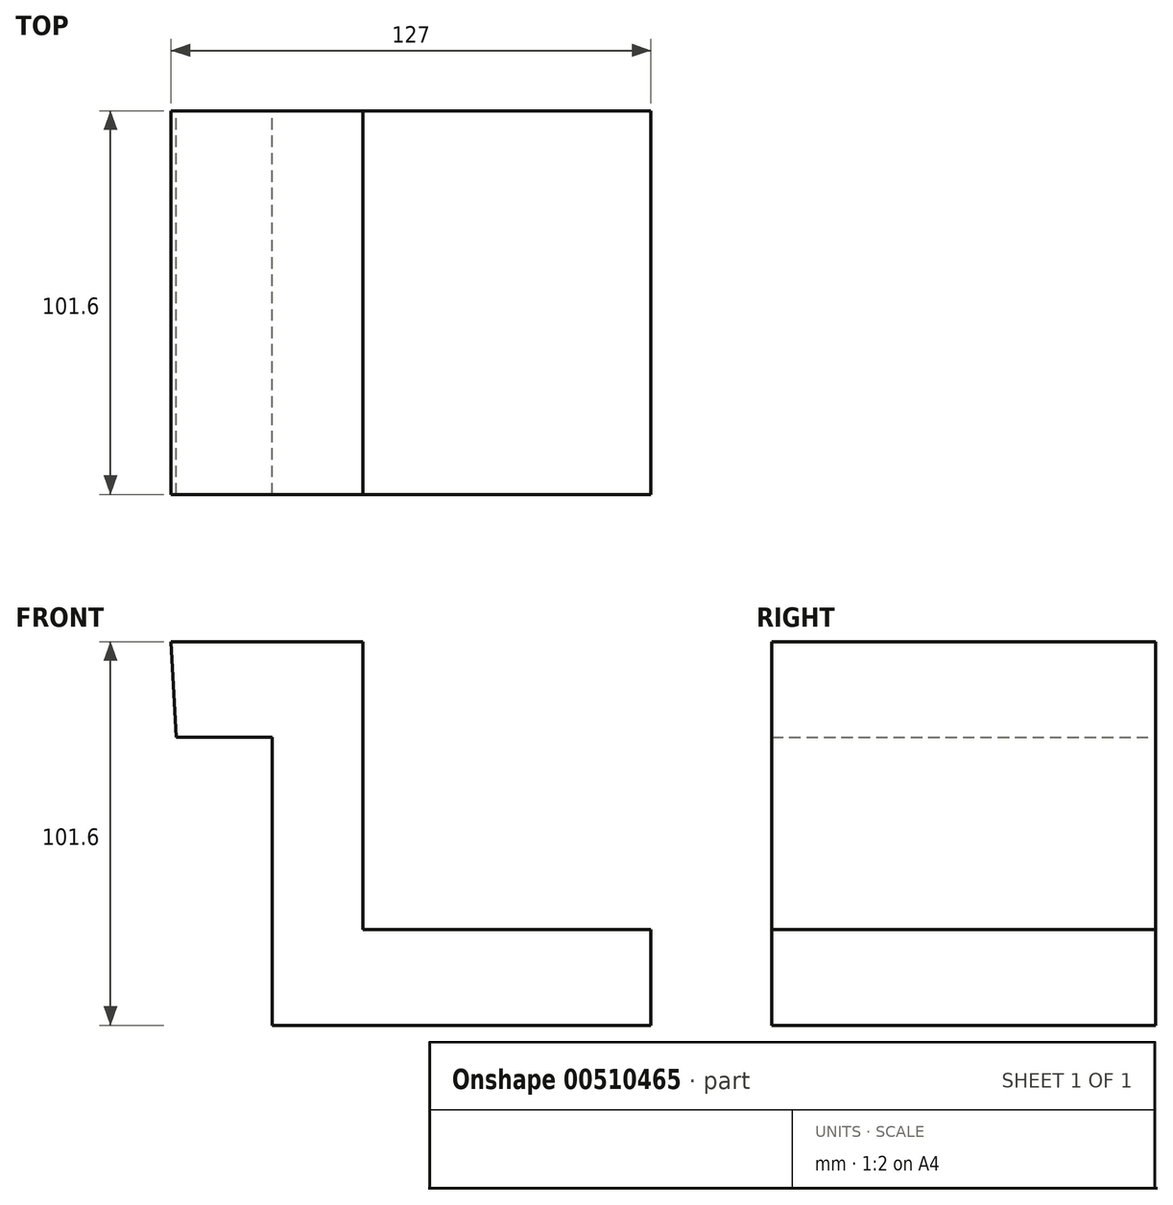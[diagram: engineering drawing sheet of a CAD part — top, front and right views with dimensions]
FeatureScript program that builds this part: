
annotation { "Feature Type Name" : "Feature", "Feature Type Description" : "" }
export const myFeature = defineFeature(function(context is Context, id is Id, definition is map)
    precondition{}
    {
        {
            var Q0;
            Q0=qCreatedBy(makeId("Front.planeOp"),FACE);
            var sketch = newSketch(context, id + "F0", { "sketchPlane" : qUnion([Q0])});
            skLineSegment(sketch, "E0", {"start": v(0, 0) * mm, "end": v(-76.2, 0) * mm});
            skLineSegment(sketch, "E1", {"start": v(-76.2, 0) * mm, "end": v(-76.2, 76.2) * mm});
            skLineSegment(sketch, "E2", {"start": v(-76.2, 76.2) * mm, "end": v(-127, 76.2) * mm});
            skLineSegment(sketch, "E3", {"start": v(-127, 76.2) * mm, "end": v(-125.63, 50.84) * mm});
            skLineSegment(sketch, "E4", {"start": v(-125.63, 50.84) * mm, "end": v(-100.23, 50.84) * mm});
            skLineSegment(sketch, "E5", {"start": v(-100.23, 50.84) * mm, "end": v(-100.23, 0) * mm});
            skLineSegment(sketch, "E6", {"start": v(-100.23, 0) * mm, "end": v(-100.23, -25.4) * mm});
            skLineSegment(sketch, "E7", {"start": v(-100.23, -25.4) * mm, "end": v(0, -25.4) * mm});
            skLineSegment(sketch, "E8", {"start": v(0, 0) * mm, "end": v(0, -25.4) * mm});
            skSolve(sketch);
        }
        {
            var Q0;
            Q0 = qSketchRegion(id + "F0", true);
            extrude(context, id + "F1", {"entities" : qUnion([Q0]), "depth" : 101.6 * mm});
        }
    });
